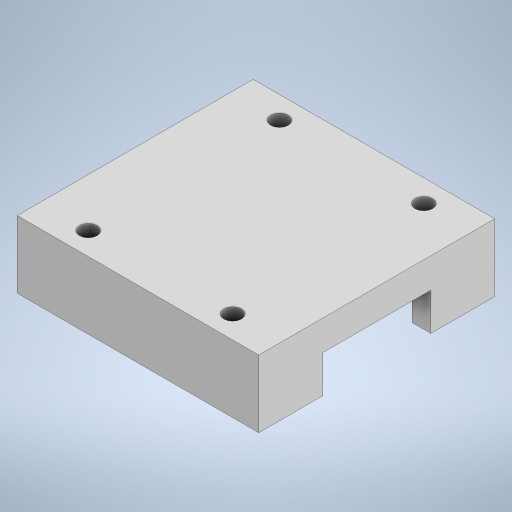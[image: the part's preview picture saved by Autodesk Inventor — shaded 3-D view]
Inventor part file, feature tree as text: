
AUTODESK INVENTOR PART (.ipt)
format: ipt  version: 2024 (Build 280153000, 153)  size: 321,024 bytes
history: native  units: in
note: dims shown in document units (in); Inventor stores cm internally (conversion verified against a paired STEP export)
features: extrude x4, projected_geometry x4, sketch x3, other x1
ambient origin geometry x8: Origin, YZ Plane, XZ Plane, XY Plane, X Axis, Y Axis, Z Axis, Center Point
bodies: Solid1 (feature_tree)
feature tree (12):
  other  "ESC_Mount.ipt"
  extrude  "Extrusion1"  Depth=0.25in TaperAngle=0.0deg
  extrude  "Extrusion2"  Depth=0.25in
  extrude  "Extrusion3"  Depth=0.25in
  extrude  "Extrusion4"  Depth=0.125in
  sketch  "Sketch2"  dims[d0=0.3937in d1=0.25in d2=0.0in]
  projected_geometry  "Projected Loop1"
  sketch  "Sketch3"  dims[d3=0.25in d4=0.25in]
  projected_geometry  "Projected Loop2"
  projected_geometry  "Projected Loop3"
  sketch  "Sketch4"  dims[d5=0.25in d6=0.25in d7=0.125in d8=0.2in d9=0.0in d10=0.1in d11=0.0in d12=0.1181in d13=0.1181in d14=0.1181in d15=0.1181in d16=0.1in d17=0.0in]
  projected_geometry  "Projected Loop4"
